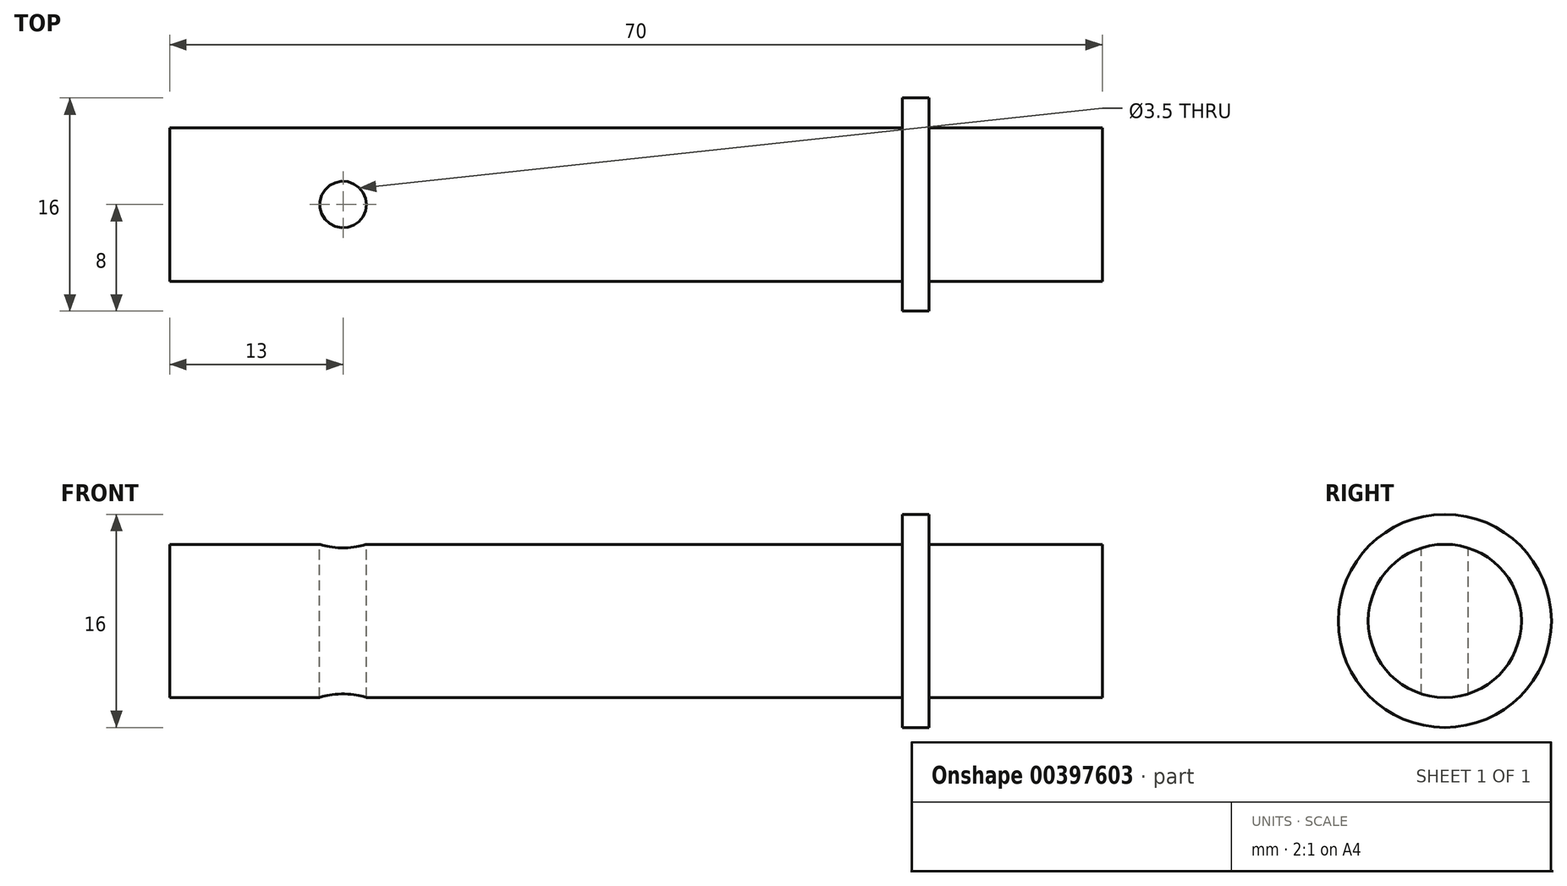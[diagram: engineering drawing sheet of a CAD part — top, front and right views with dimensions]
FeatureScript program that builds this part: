
annotation { "Feature Type Name" : "Feature", "Feature Type Description" : "" }
export const myFeature = defineFeature(function(context is Context, id is Id, definition is map)
    precondition{}
    {
        {
            var Q0;
            Q0=qCreatedBy(makeId("Right.planeOp"),FACE);
            var sketch = newSketch(context, id + "F0", { "sketchPlane" : qUnion([Q0])});
            skCircle(sketch, "E0", {"center": v(0, 0) * mm, "radius": 5.75 * mm});
            skSolve(sketch);
        }
        {
            var Q0;
            Q0=qSketchRegion(id+"F0",true);
            extrude(context, id + "F1", {"entities" : qUnion([Q0]), "depth" : 70 * mm});
        }
        {
            var Q0;
            Q0=qCreatedBy(makeId("Top.planeOp"),FACE);
            cPlane(context, id + "F2", {"entities" : qUnion([Q0]), "cplaneType" : CPlaneType.OFFSET, "offset" : 6.8 * mm, "width" : 150 * mm, "height" : 150 * mm});
        }
        {
            var Q0;
            Q0=qCreatedBy(id+"F2.planeOp",FACE);
            var sketch = newSketch(context, id + "F3", { "sketchPlane" : qUnion([Q0])});
            skLineSegment(sketch, "E1", {"start": v(0, 0) * mm, "end": v(70, 0) * mm});
            skLineSegment(sketch, "E2", {"start": v(0, 0) * mm, "end": v(13, 0) * mm});
            skCircle(sketch, "E3", {"center": v(13, 0) * mm, "radius": 1.75 * mm});
            skLineSegment(sketch, "E4", {"start": v(70, 0) * mm, "end": v(55, 0) * mm});
            skSolve(sketch);
        }
        {
            var Q0;
            Q0=qSketchRegion(id+"F3",true);
            extrude(context, id + "F4", {"entities" : qUnion([Q0]), "operationType" : NewBodyOperationType.REMOVE, "oppositeDirection" : true, "depth" : 25 * mm});
        }
        {
            var Q0;
            Q0=qCreatedBy(makeId("Right.planeOp"),FACE);
            cPlane(context, id + "F5", {"entities" : qUnion([Q0]), "cplaneType" : CPlaneType.OFFSET, "offset" : 55 * mm, "width" : 150 * mm, "height" : 150 * mm});
        }
        {
            var Q0;
            Q0=qCreatedBy(id+"F5.planeOp",FACE);
            var sketch = newSketch(context, id + "F6", { "sketchPlane" : qUnion([Q0])});
            skCircle(sketch, "E5", {"center": v(0, 0) * mm, "radius": 8 * mm});
            skSolve(sketch);
        }
        {
            var Q0;
            Q0=qSketchRegion(id+"F6",true);
            extrude(context, id + "F7", {"entities" : qUnion([Q0]), "operationType" : NewBodyOperationType.ADD, "depth" : 2 * mm});
        }
    });
